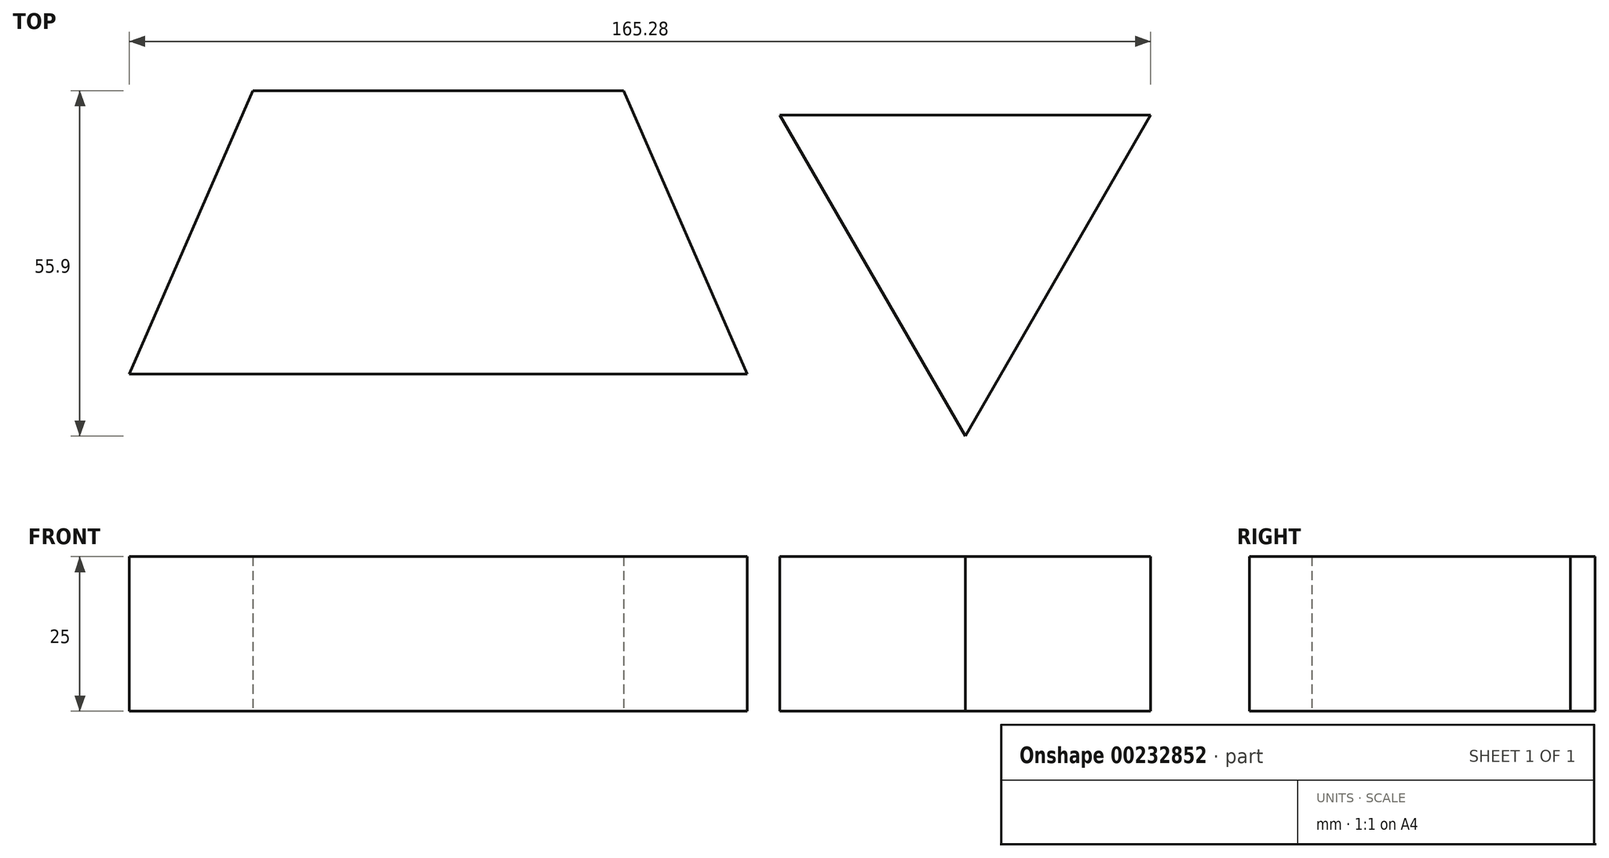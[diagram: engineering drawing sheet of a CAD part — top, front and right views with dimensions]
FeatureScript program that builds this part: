
annotation { "Feature Type Name" : "Feature", "Feature Type Description" : "" }
export const myFeature = defineFeature(function(context is Context, id is Id, definition is map)
    precondition{}
    {
        {
            var Q0;
            Q0=qCreatedBy(makeId("Top.planeOp"),FACE);
            var sketch = newSketch(context, id + "F0", { "sketchPlane" : qUnion([Q0])});
            skLineSegment(sketch, "E0", {"start": v(-67.26, 59.8) * mm, "end": v(-7.26, 59.8) * mm});
            skLineSegment(sketch, "E1", {"start": v(-7.26, 59.8) * mm, "end": v(12.74, 13.97) * mm});
            skLineSegment(sketch, "E2", {"start": v(12.74, 13.97) * mm, "end": v(-87.26, 13.97) * mm});
            skLineSegment(sketch, "E3", {"start": v(-67.26, 59.8) * mm, "end": v(-87.26, 13.97) * mm});
            skLineSegment(sketch, "E4", {"start": v(18.02, 55.85) * mm, "end": v(78.02, 55.85) * mm});
            skLineSegment(sketch, "E5", {"start": v(78.02, 55.85) * mm, "end": v(78.02, 54.35) * mm});
            skLineSegment(sketch, "E6", {"start": v(78.02, 55.85) * mm, "end": v(48.02, 3.89) * mm});
            skLineSegment(sketch, "E7", {"start": v(18.02, 55.85) * mm, "end": v(48.02, 3.89) * mm});
            skLineSegment(sketch, "E8", {"start": v(-42.24, -56.79) * mm, "end": v(37.76, -56.79) * mm});
            skLineSegment(sketch, "E9", {"start": v(-42.24, -56.79) * mm, "end": v(-18.3, 9) * mm});
            skLineSegment(sketch, "E10", {"start": v(-18.3, 9) * mm, "end": v(6.87, -3.28) * mm});
            skLineSegment(sketch, "E11", {"start": v(37.76, -56.79) * mm, "end": v(67.76, -4.82) * mm});
            skSolve(sketch);
        }
        {
            var Q0;
            Q0 = qSketchRegion(id + "F0", true);
            extrude(context, id + "F1", {"entities" : qUnion([Q0]), "depth" : 25 * mm});
        }
    });
